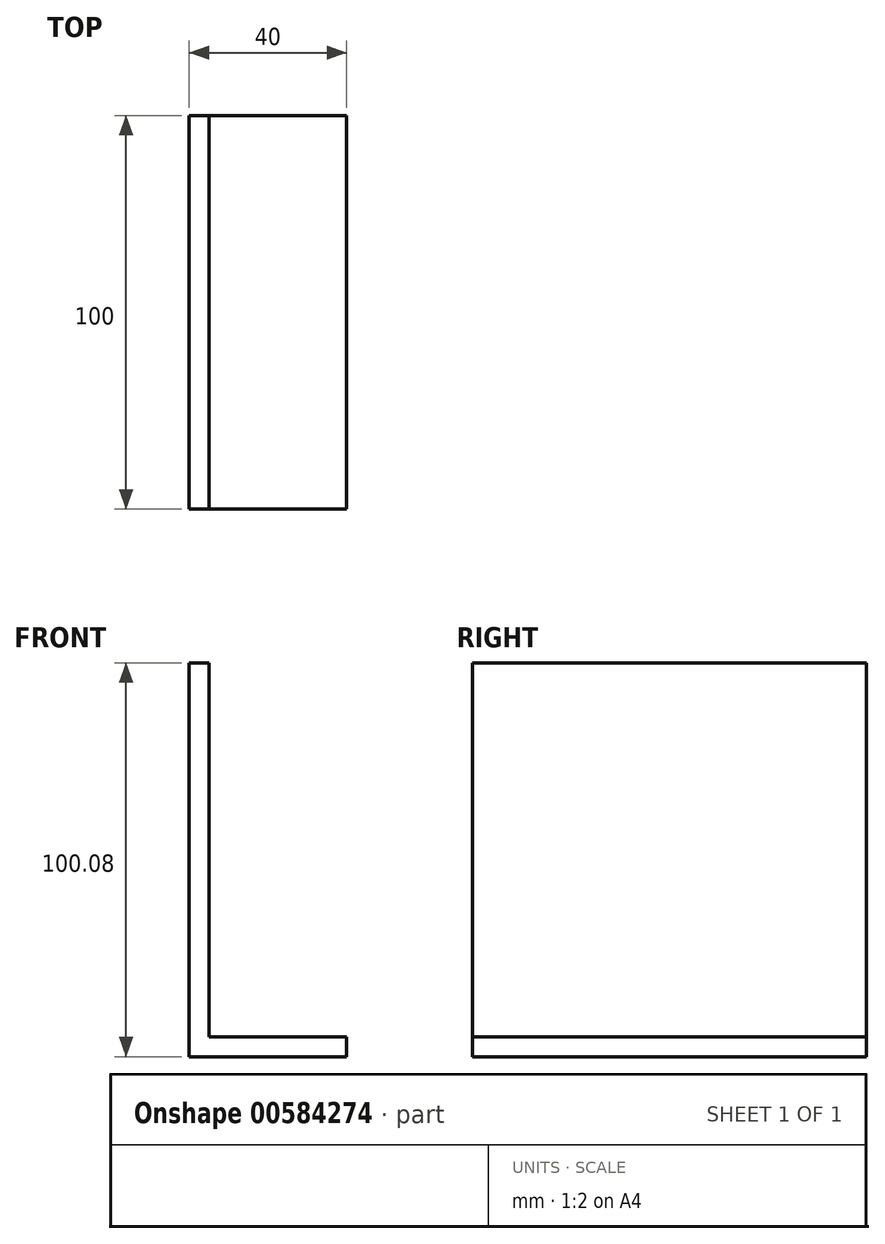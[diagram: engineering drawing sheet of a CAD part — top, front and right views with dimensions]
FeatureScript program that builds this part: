
annotation { "Feature Type Name" : "Feature", "Feature Type Description" : "" }
export const myFeature = defineFeature(function(context is Context, id is Id, definition is map)
    precondition{}
    {
        {
            var Q0;
            Q0=qCreatedBy(makeId("Front.planeOp"),FACE);
            var sketch = newSketch(context, id + "F0", { "sketchPlane" : qUnion([Q0])});
            skLineSegment(sketch, "E0", {"start": v(12.2, 81.7) * mm, "end": v(12.2, -18.3) * mm});
            skLineSegment(sketch, "E1", {"start": v(12.2, -18.3) * mm, "end": v(52.2, -18.3) * mm});
            skLineSegment(sketch, "E2", {"start": v(52.2, -18.3) * mm, "end": v(52.2, -13.3) * mm});
            skLineSegment(sketch, "E3", {"start": v(52.2, -13.3) * mm, "end": v(17.2, -13.3) * mm});
            skLineSegment(sketch, "E4", {"start": v(17.2, -13.3) * mm, "end": v(17.2, 81.78) * mm});
            skLineSegment(sketch, "E5", {"start": v(17.2, 81.78) * mm, "end": v(12.2, 81.7) * mm});
            skSolve(sketch);
        }
        {
            var Q0;
            Q0=makeQuery(id+"F0.imprint","IMPRINT",FACE,{"disambiguationData":[TD([[makeQuery(id+"F0.imprint","IMPRINT",EDGE,{"derivedFrom":sQuery(id+"F0.wireOp",EDGE,"E0")}),1.0]])]});
            extrude(context, id + "F1", {"entities" : qUnion([Q0]), "depth" : 100 * mm, "offsetDistance" : 25 * mm});
        }
    });
